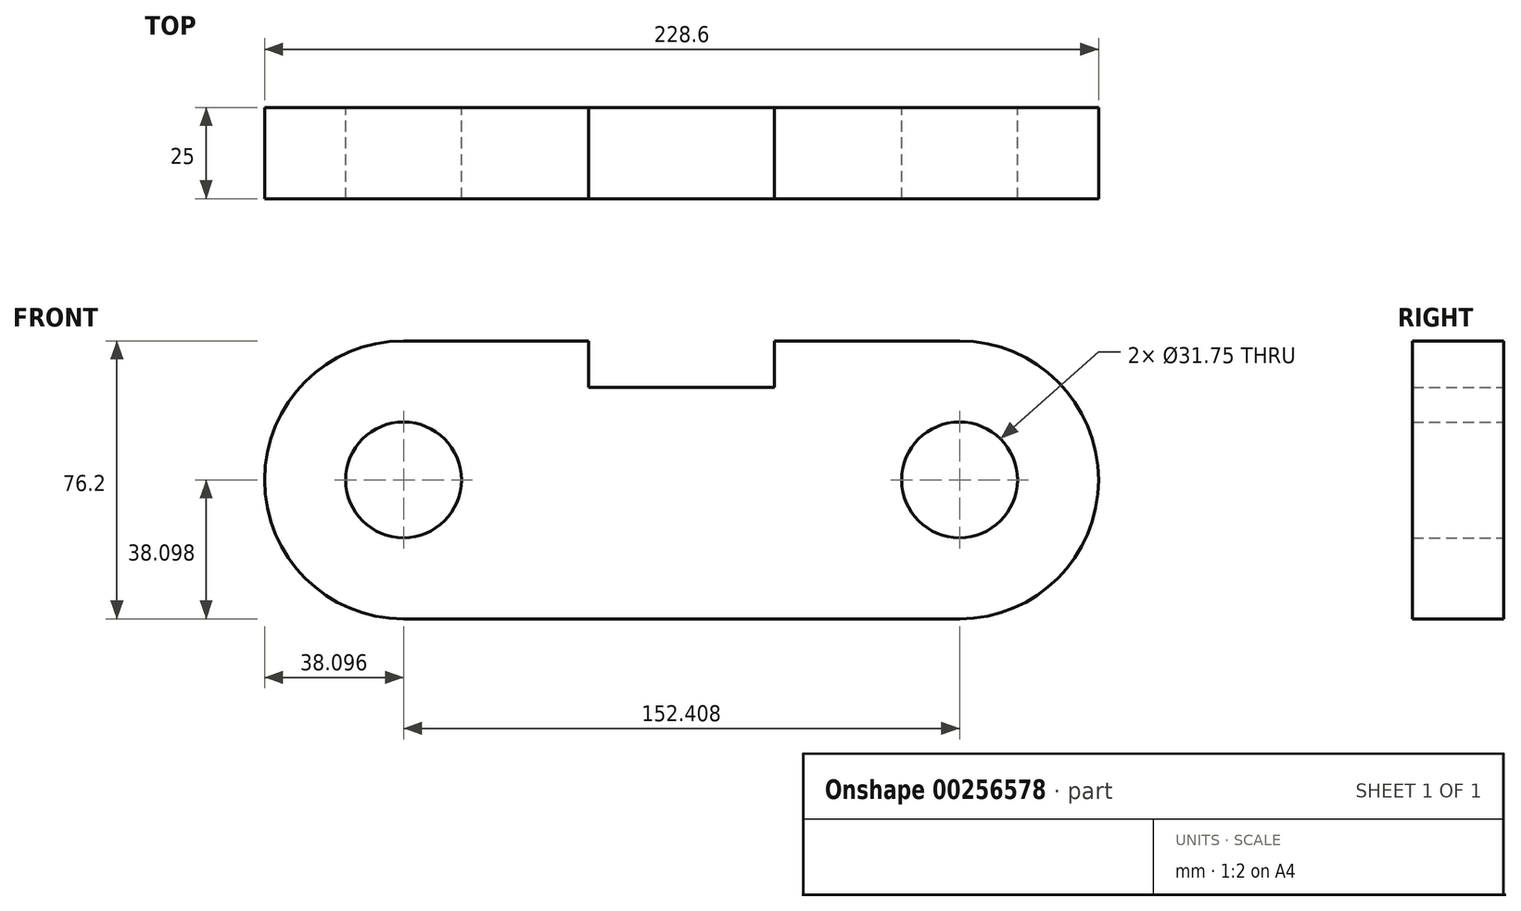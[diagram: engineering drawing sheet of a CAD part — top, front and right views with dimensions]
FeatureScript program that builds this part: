
annotation { "Feature Type Name" : "Feature", "Feature Type Description" : "" }
export const myFeature = defineFeature(function(context is Context, id is Id, definition is map)
    precondition{}
    {
        {
            var Q0;
            Q0=qCreatedBy(makeId("Front.planeOp"),FACE);
            var sketch = newSketch(context, id + "F0", { "sketchPlane" : qUnion([Q0])});
            skCircle(sketch, "E0", {"center": v(119.45, 6.94) * mm, "radius": 15.88 * mm});
            skCircle(sketch, "E1", {"center": v(-32.95, 6.94) * mm, "radius": 15.88 * mm});
            skLineSegment(sketch, "E2", {"start": v(-78.05, 6.94) * mm, "end": v(-71.05, 6.94) * mm});
            skCircle(sketch, "E3", {"center": v(119.45, 6.94) * mm, "radius": 38.1 * mm});
            skPoint(sketch, "E4.orphan", {"position": v(119.45, 42.97) * mm});
            skLineSegment(sketch, "E5", {"start": v(119.45, 6.94) * mm, "end": v(119.45, -8.94) * mm});
            skLineSegment(sketch, "E6", {"start": v(119.45, -31.16) * mm, "end": v(119.45, -29.1) * mm});
            skLineSegment(sketch, "E7", {"start": v(119.45, 45.04) * mm, "end": v(119.45, 42.97) * mm});
            skCircle(sketch, "E8", {"center": v(-32.95, 6.94) * mm, "radius": 38.1 * mm});
            skPoint(sketch, "E9.orphan", {"position": v(-32.95, 41.43) * mm});
            skLineSegment(sketch, "E10", {"start": v(-32.95, -27.56) * mm, "end": v(-32.95, -31.16) * mm});
            skPoint(sketch, "E11.start.orphan", {"position": v(-32.95, -27.56) * mm});
            skPoint(sketch, "E12.trimOffspring.end.orphan", {"position": v(119.45, -29.1) * mm});
            skLineSegment(sketch, "E13", {"start": v(-32.95, 45.04) * mm, "end": v(17.85, 45.04) * mm});
            skLineSegment(sketch, "E14", {"start": v(17.85, 45.04) * mm, "end": v(17.85, 32.34) * mm});
            skLineSegment(sketch, "E15", {"start": v(68.65, 32.34) * mm, "end": v(17.85, 32.34) * mm});
            skLineSegment(sketch, "E16", {"start": v(68.65, 32.34) * mm, "end": v(68.65, 45.04) * mm});
            skLineSegment(sketch, "E17", {"start": v(68.65, 45.04) * mm, "end": v(119.45, 45.04) * mm});
            skLineSegment(sketch, "E18.trimOffspring", {"start": v(119.45, -8.94) * mm, "end": v(119.45, 6.94) * mm});
            skLineSegment(sketch, "E19.trimOffspring", {"start": v(119.45, 22.81) * mm, "end": v(119.45, 6.94) * mm});
            skPoint(sketch, "E20.orphan", {"position": v(119.45, 68.03) * mm});
            skLineSegment(sketch, "E21.trimOffspring", {"start": v(119.45, -29.1) * mm, "end": v(119.45, -31.16) * mm});
            skLineSegment(sketch, "E22", {"start": v(-32.95, -31.16) * mm, "end": v(119.45, -31.16) * mm});
            skSolve(sketch);
        }
        {
            var Q0;
            {var subQ0=sQuery(id+"F0.wireOp",EDGE,"E13");Q0=makeQuery(id+"F0.imprint","IMPRINT",FACE,{"disambiguationData":[TD([[makeQuery(id+"F0.imprint","IMPRINT",EDGE,{"derivedFrom":subQ0}),-1.0]])]});}
            var Q1;
            Q1=makeQuery(id+"F0.imprint","IMPRINT",FACE,{"disambiguationData":[TD([[makeQuery(id+"F0.imprint","IMPRINT",EDGE,{"derivedFrom":sQuery(id+"F0.wireOp",EDGE,"E1")}),-1.0]])]});
            var Q2;
            {var subQ0=sQuery(id+"F0.wireOp",EDGE,"E0");var subQ1=makeQuery(id+"F0.imprint","INTERSECT",VERTEX,{"derivedFrom":[subQ0,sQuery(id+"F0.wireOp",EDGE,"E18.trimOffspring")]});Q2=makeQuery(id+"F0.imprint","IMPRINT",FACE,{"disambiguationData":[TD([[makeQuery(id+"F0.imprint","IMPRINT",EDGE,{"disambiguationData":[TD([[subQ1,1.0]])],"derivedFrom":subQ0}),-1.0]])]});}
            extrude(context, id + "F1", {"entities" : qUnion([Q0, Q1, Q2]), "depth" : 25 * mm});
        }
    });
